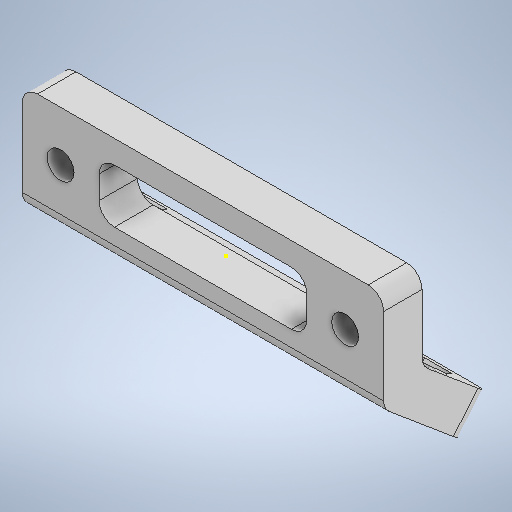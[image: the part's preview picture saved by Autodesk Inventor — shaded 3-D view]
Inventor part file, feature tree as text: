
AUTODESK INVENTOR PART (.ipt)
format: ipt  version: 2025.1 (Build 291241000, 241)  size: 363,008 bytes
history: native  units: mm
features: sketch x7, extrude x6, other x3, fillet x3
ambient origin geometry x8: Origin, YZ Plane, XZ Plane, XY Plane, X Axis, Y Axis, Z Axis, Center Point
bodies: Body1 (feature_tree)
feature tree (19):
  other  "ソリッド1"
  extrude  "押し出し1"  Depth=3.5mm
  extrude  "押し出し2"  Depth=3.5mm
  extrude  "押し出し3"  Depth=37.0mm
  extrude  "押し出し5"  Depth=18.5mm
  fillet  "フィレット2"  Radius=10.0mm
  extrude  "押し出し6"  Depth=10.0mm
  fillet  "フィレット3"  Radius=13.0mm
  extrude  "押し出し7"  Depth=5.0mm TaperAngle=0.0deg
  fillet  "フィレット4"  Radius=3.0mm
  sketch  "スケッチ8"
  sketch  "スケッチ1"
  sketch  "スケッチ2"
  sketch  "スケッチ3"
  other  "スケッチ円形状パターン1"
  sketch  "スケッチ5"
  sketch  "スケッチ6"
  sketch  "スケッチ7"
  other  "スケッチ円形状パターン2"
